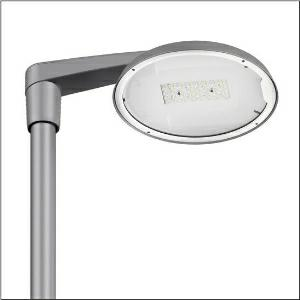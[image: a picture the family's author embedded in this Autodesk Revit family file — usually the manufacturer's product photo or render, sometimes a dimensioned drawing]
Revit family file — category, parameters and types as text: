
# Revit family: dl_r__50_iq_mini___st0_5a_5xa248b31f08he_0d04
name_source: partatom
category: Lighting Fixtures
units: mm (PartAtom-declared; Revit-internal decimal feet)

## family parameters
Cut with Voids When Loaded = No
Host = Face
Light Source = No
Part Type = Normal
Room Calculation Point = No
Round Connector Dimension = Use Diameter
Shared = No

## types (1)
- --- (1 x LED, 9400 lm, 68.6 W, 3000K)
    Apparent Load = 69 VA
    CIE Flux Codes = 41 75 97 100 100
    Color Rendering = 70
    Color Temperature = 3000K
    Default Elevation = 1800 mm
    Description = DL® 50 iQ mini, mast luminaire, primary light control with lens, of PMMA, primary optical cover: cover, of toughened safety glass, transparent, light distribution: ST0.5a, light emission: direct distribution, primary light characteristic: asymmetric, installation type: side-entry, post-top, LED, High Power LED, rated luminous flux: 9.400lm, luminous efficacy: 137lm/W, light colour: 730, colour temperature: 3000K, control gear: iQ Street-Remote, control: optimised constant luminous flux control (CLO 2.0), Desk-Remote (wireless, voltage-free reading and setting of iQ features in the workshop via application-optimized NFC function/RFID function), Light-Fading, Smart-Wire, Night-Set, Lumen-Switch, Temp-Guard, Auto-Match, Street-Remote, mains connection: 230..240V, AC, 50/60Hz, connection cable pre-assembled, cable length: 8,5m, start of lifetime: 69W, end of service life: 72W, reduction: 30W, luminaire housing, of diecast aluminium, powder-coated, Siteco® metallic grey (DB 702S), inclination adjustable: 0°, 5°, 10° (post-top) | 0°, -5°, -10°, -15° (side-entry), please order mast post-top element or mast side-entry element separately, diameter: 500mm, height: 115mm, post-top: for spigot size d x l = 76 x 100mm; with reducer (optional accessory) 60 x 100mm | side-entry: for spigot size d x l = 60 x 100mm; with reducer (optional accessory) 42 x 100mm, mounting height: 4..6m, protection rating (complete): IP66, insulation class (complete): insulation class II (safety insulation), certification: CE, ENEC, ENEC+, VDE, impact resistance: IK08, permissible operating ambient temperature for outdoor applications: -25..+40°C, standard-compliant lighting for roads and squares, packaging unit: 1 piece

Light Distribution: ST0.5a
    Height = 115 mm
    Lamp = 1 x LED
    Lamp Light Flux = 9400 lm
    Lamp Power = 68.6 W
    Lamp count = 1
    Length = 500 mm
    Luminous efficacy = 137 lm/W
    Manufacturer = Siteco
    ModVariant = No
    Model = 5XA248B31F08HE
    Number of Poles = 1
    OnlyDefault = Yes
    Power Factor = 1
    Product Name = DL® 50 iQ mini | ST0.5a
    Product group = mast luminaire | pylon top
    ProductGroupID = 6100
    Protection Class = Protection class II
    Protection Degree = IP 66
    RLX_Detail_Level = 1
    RLX_Emergency_Light_Flux = 0 lm
    RLX_Emergency_Type = 0
    RLX_Emergency_Type_DB = No
    RlxData = <blob elided: 126633 chars, md5=810315d2>
    Socket = socket
    Standby Power = 0 W
    System Light Flux = 9400 lm
    System Power = 69 W
    Type Comments = factory setting: luminous flux: 100 % | dim-lin: 254 | 693 mA
    Type Image = l_1251794.jpg
    URL = http://relux.com
    VarID = @adj_143224
    Voltage = 0 V
    Weight = 0.00 kg
    Width = 0 mm  [stored 0 ft]

note: [stored X ft] marks values corroborated as IEEE doubles in the binary element streams (Revit-internal decimal feet)

## geometry (parser evidence)
native form markers: Blend x4, Sweep x11
no freeform markers — native parametric forms only
